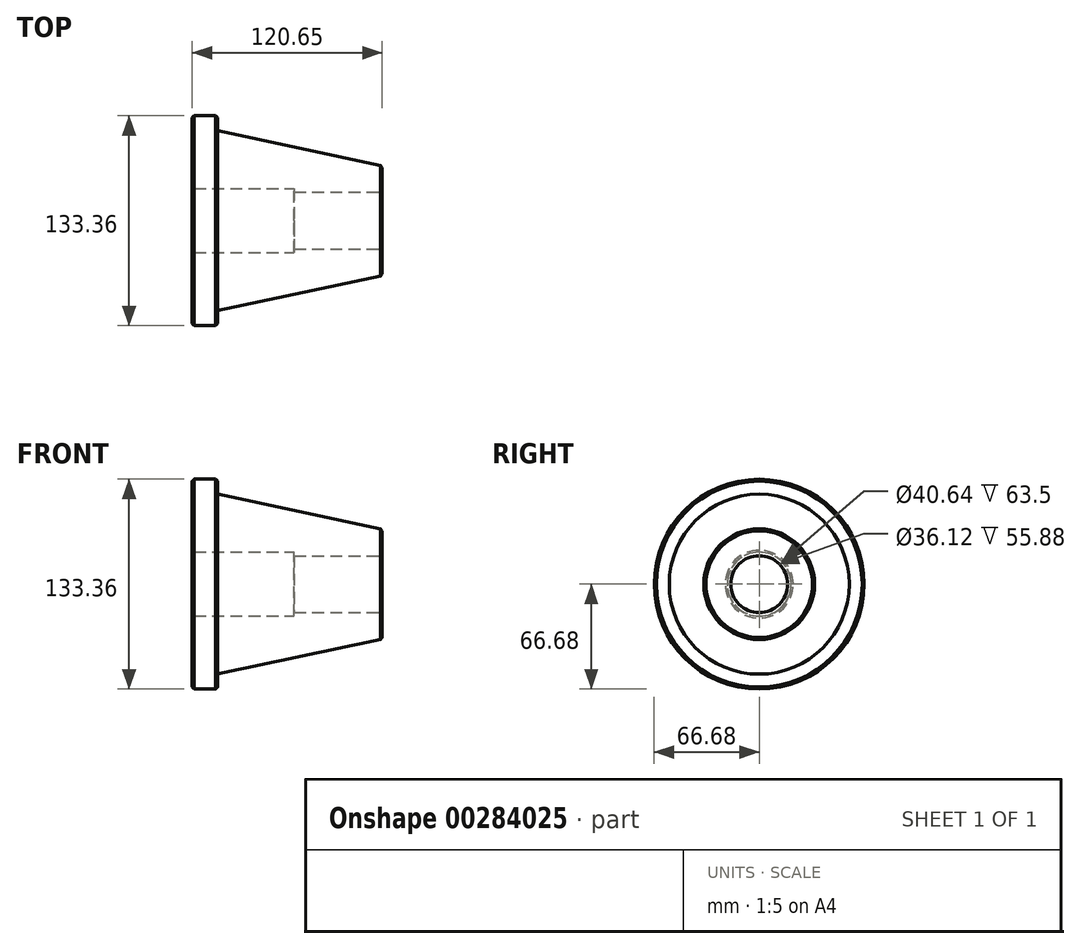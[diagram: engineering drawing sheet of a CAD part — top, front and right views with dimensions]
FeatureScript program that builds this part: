
annotation { "Feature Type Name" : "Feature", "Feature Type Description" : "" }
export const myFeature = defineFeature(function(context is Context, id is Id, definition is map)
    precondition{}
    {
        {
            var Q0;
            Q0=qCreatedBy(makeId("Front.planeOp"),FACE);
            var sketch = newSketch(context, id + "F0", { "sketchPlane" : qUnion([Q0])});
            skLineSegment(sketch, "E0", {"start": v(0, 34.92) * mm, "end": v(-104.56, 57.15) * mm});
            skLineSegment(sketch, "E1", {"start": v(-104.56, 57.15) * mm, "end": v(-104.56, 66.67) * mm});
            skLineSegment(sketch, "E2", {"start": v(-104.56, 66.67) * mm, "end": v(-120.65, 66.67) * mm});
            skLineSegment(sketch, "E3", {"start": v(-120.65, 66.67) * mm, "end": v(-120.65, 20.32) * mm});
            skLineSegment(sketch, "E4", {"start": v(-120.65, 20.32) * mm, "end": v(-55.88, 20.32) * mm});
            skLineSegment(sketch, "E5", {"start": v(0, 0) * mm, "end": v(0, 34.92) * mm});
            skLineSegment(sketch, "E6", {"start": v(28.33, 0) * mm, "end": v(-139.65, 0) * mm, "construction": true});
            skLineSegment(sketch, "E7", {"start": v(-55.88, 20.32) * mm, "end": v(-55.88, 0) * mm});
            skLineSegment(sketch, "E8", {"start": v(-55.88, 0) * mm, "end": v(0, 0) * mm});
            skSolve(sketch);
        }
        {
            var Q0;
            Q0=makeQuery(id+"F0.imprint","IMPRINT",FACE,{"disambiguationData":[TD([[makeQuery(id+"F0.imprint","IMPRINT",EDGE,{"derivedFrom":sQuery(id+"F0.wireOp",EDGE,"E0")}),1.0]])]});
            var Q1;
            Q1=sQuery(id+"F0.wireOp",EDGE,"E6");
            revolve(context, id + "F1", {"entities" : qUnion([Q0]), "axis" : qUnion([Q1]), "revolveType" : RevolveType.FULL});
        }
        {
            var Q0;
            Q0=makeQuery(id+"F1.opRevolve","SWEPT_FACE",FACE,{"disambiguationData":[OSD([sQuery(id+"F0.wireOp",EDGE,"E5")])]});
            var sketch = newSketch(context, id + "F2", { "sketchPlane" : qUnion([Q0])});
            skCircle(sketch, "E9", {"center": v(0, 0) * mm, "radius": 19.05 * mm});
            skSolve(sketch);
        }
        {
            var Q0;
            Q0=sQuery(id+"F2.wireOp",VERTEX,"E9.center");
            var Q1;
            Q1=makeQuery(id+"F1.opRevolve","SWEPT_BODY",BODY,{"disambiguationData":[OSD([sQuery(id+"F0.wireOp",EDGE,"E0"),sQuery(id+"F0.wireOp",EDGE,"E1"),sQuery(id+"F0.wireOp",EDGE,"E2"),sQuery(id+"F0.wireOp",EDGE,"E3"),sQuery(id+"F0.wireOp",EDGE,"E4"),sQuery(id+"F0.wireOp",EDGE,"E5"),sQuery(id+"F0.wireOp",EDGE,"E7"),sQuery(id+"F0.wireOp",EDGE,"E8")])]});
            hole(context, id + "F3", {"style" : HoleStyle.SIMPLE, "endStyle" : HoleEndStyle.THROUGH, "standardTappedOrClearance" : lookupTablePath({ "standard" : "ANSI", "engagement" : "75%", "pitch" : "12 tpi", "size" : "1 1/2", "type" : "Tapped" }), "standardBlindInLast" : lookupTablePath({ "standard" : "ANSI", "engagement" : "75%", "pitch" : "12 tpi", "size" : "1 1/2", "type" : "Tapped" }), "holeDiameter" : 36.12 * mm, "showTappedDepth" : true, "tappedDepth" : 24.33 * mm, "tapClearance" : 3, "locations" : qUnion([Q0]), "scope" : qUnion([Q1]), "majorDiameter" : 38.1 * mm});
        }
        {
            var Q0;
            Q0=makeQuery(id+"F1.opRevolve","SWEPT_EDGE",EDGE,{"disambiguationData":[OSD([sQuery(id+"F0.wireOp",EDGE,"E2"),sQuery(id+"F0.wireOp",EDGE,"E3")])]});
            var Q1;
            Q1=makeQuery(id+"F1.opRevolve","SWEPT_EDGE",EDGE,{"disambiguationData":[OSD([sQuery(id+"F0.wireOp",EDGE,"E3"),sQuery(id+"F0.wireOp",EDGE,"E4")])]});
            var Q2;
            Q2=makeQuery(id+"F1.opRevolve","SWEPT_EDGE",EDGE,{"disambiguationData":[OSD([sQuery(id+"F0.wireOp",EDGE,"E1"),sQuery(id+"F0.wireOp",EDGE,"E2")])]});
            var Q3;
            Q3=makeQuery(id+"F1.opRevolve","SWEPT_EDGE",EDGE,{"disambiguationData":[OSD([sQuery(id+"F0.wireOp",EDGE,"E0"),sQuery(id+"F0.wireOp",EDGE,"E5")])]});
            var Q4;
            Q4=makeQuery(id+"F3.hole-0.boolean.opBoolean","COPY",EDGE,{"derivedFrom":makeQuery(id+"F3.hole-0.opRevolve","SWEPT_EDGE",EDGE,{"disambiguationData":[OSD([sQuery(id+"F3.hole-0.sketch.wireOp",EDGE,"core_line_2"),sQuery(id+"F3.hole-0.sketch.wireOp",EDGE,"core_line_3")])]})});
            chamfer(context, id + "F4", {"entities" : qUnion([Q0, Q1, Q2, Q3, Q4]), "width" : 1.27 * mm, "tangentPropagation" : true});
        }
    });
